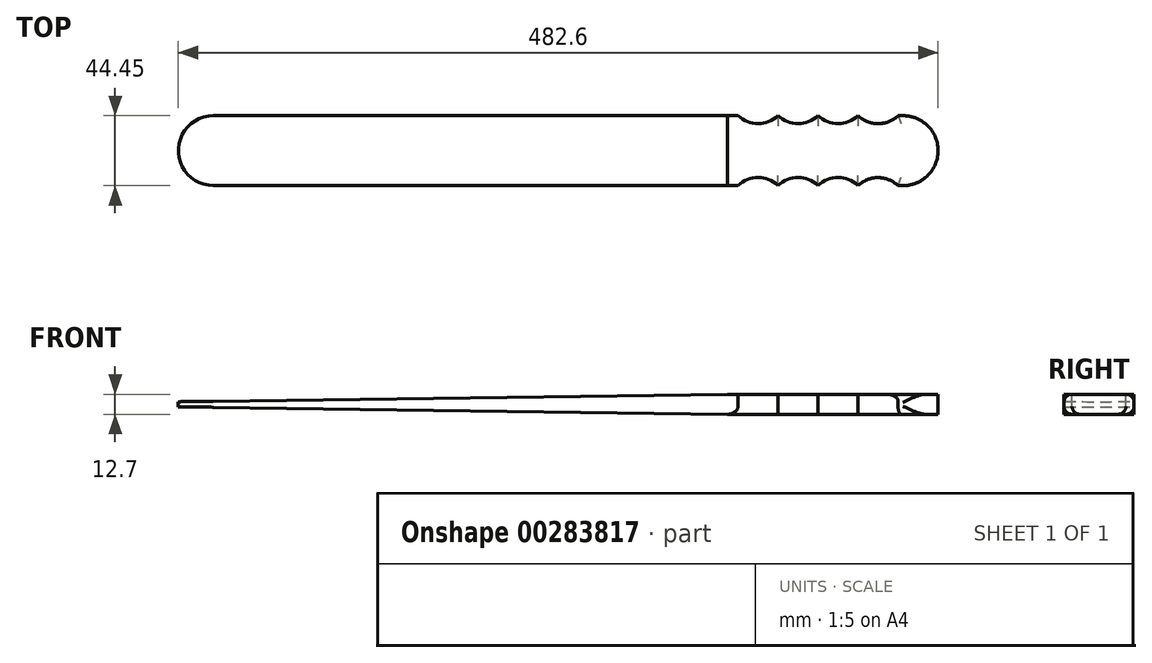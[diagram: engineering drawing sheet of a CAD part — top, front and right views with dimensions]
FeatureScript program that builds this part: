
annotation { "Feature Type Name" : "Feature", "Feature Type Description" : "" }
export const myFeature = defineFeature(function(context is Context, id is Id, definition is map)
    precondition{}
    {
        {
            var Q0;
            Q0=qCreatedBy(makeId("Front.planeOp"),FACE);
            var sketch = newSketch(context, id + "F0", { "sketchPlane" : qUnion([Q0])});
            skLineSegment(sketch, "E0", {"start": v(482.6, 6.35) * mm, "end": v(482.6, 0) * mm});
            skLineSegment(sketch, "E1.bottom", {"start": v(482.6, 6.35) * mm, "end": v(0, 6.35) * mm});
            skLineSegment(sketch, "E1.top", {"start": v(482.6, 0) * mm, "end": v(0, 0) * mm, "construction": true});
            skLineSegment(sketch, "E2", {"start": v(0, 6.35) * mm, "end": v(0, 0) * mm});
            skLineSegment(sketch, "E3.MirrorCS", {"start": v(482.6, -6.35) * mm, "end": v(482.6, 0) * mm});
            skLineSegment(sketch, "E4.MirrorCS", {"start": v(0, -6.35) * mm, "end": v(0, 0) * mm});
            skLineSegment(sketch, "E5.MirrorCS", {"start": v(482.6, -6.35) * mm, "end": v(0, -6.35) * mm});
            skSolve(sketch);
        }
        {
            var Q0;
            Q0 = qSketchRegion(id + "F0", true);
            extrude(context, id + "F1", {"entities" : qUnion([Q0]), "depth" : 44.45 * mm});
        }
        {
            var Q0;
            Q0=makeQuery(id+"F1.opExtrude","SWEPT_FACE",FACE,{"disambiguationData":[OSD([sQuery(id+"F0.wireOp",EDGE,"E1.bottom")])]});
            var sketch = newSketch(context, id + "F2", { "sketchPlane" : qUnion([Q0])});
            skLineSegment(sketch, "E6", {"start": v(355.6, 0) * mm, "end": v(355.6, -44.45) * mm, "construction": true});
            skArc(sketch, "E7", {"start": v(355.6, 0) * mm, "mid": v(368.3, -5.08) * mm, "end": v(381, 0) * mm});
            skLineSegment(sketch, "E8", {"start": v(355.6, -22.23) * mm, "end": v(482.6, -22.23) * mm, "construction": true});
            skArc(sketch, "E9.MirrorCS", {"start": v(355.6, -44.45) * mm, "mid": v(368.3, -39.37) * mm, "end": v(381, -44.45) * mm});
            skArc(sketch, "E10.1.0.0", {"start": v(381, 0) * mm, "mid": v(393.7, -5.08) * mm, "end": v(406.4, 0) * mm});
            skArc(sketch, "E10.1.0.1", {"start": v(381, -44.45) * mm, "mid": v(393.7, -39.37) * mm, "end": v(406.4, -44.45) * mm});
            skArc(sketch, "E10.2.0.0", {"start": v(406.4, 0) * mm, "mid": v(419.1, -5.08) * mm, "end": v(431.8, 0) * mm});
            skArc(sketch, "E10.2.0.1", {"start": v(406.4, -44.45) * mm, "mid": v(419.1, -39.37) * mm, "end": v(431.8, -44.45) * mm});
            skArc(sketch, "E10.3.0.0", {"start": v(431.8, 0) * mm, "mid": v(444.5, -5.08) * mm, "end": v(457.2, 0) * mm});
            skArc(sketch, "E10.3.0.1", {"start": v(431.8, -44.45) * mm, "mid": v(444.5, -39.37) * mm, "end": v(457.2, -44.45) * mm});
            skLineSegment(sketch, "E10.direction1", {"start": v(368.3, -57.79) * mm, "end": v(393.7, -57.79) * mm, "construction": true});
            skLineSegment(sketch, "E11", {"start": v(355.6, 0) * mm, "end": v(457.2, 0) * mm});
            skLineSegment(sketch, "E12.MirrorCS", {"start": v(355.6, -44.45) * mm, "end": v(457.2, -44.45) * mm});
            skSolve(sketch);
        }
        {
            var Q0;
            Q0 = qSketchRegion(id + "F2", true);
            extrude(context, id + "F3", {"entities" : qUnion([Q0]), "operationType" : NewBodyOperationType.REMOVE, "endBound" : BoundingType.THROUGH_ALL, "oppositeDirection" : true, "depth" : 25.4 * mm});
        }
        {
            var Q0;
            Q0=makeQuery(id+"F3.boolean.opBoolean","COPY",EDGE,{"derivedFrom":makeQuery(id+"F3.opExtrude","CAP_EDGE",EDGE,{"disambiguationData":[OSD([sQuery(id+"F2.wireOp",EDGE,"E9.MirrorCS")])],"isStart":true})});
            var Q1;
            Q1=makeQuery(id+"F3.boolean.opBoolean","COPY",EDGE,{"derivedFrom":makeQuery(id+"F3.opExtrude","CAP_EDGE",EDGE,{"disambiguationData":[OSD([sQuery(id+"F2.wireOp",EDGE,"E10.1.0.1")])],"isStart":true})});
            var Q2;
            Q2=makeQuery(id+"F3.boolean.opBoolean","COPY",EDGE,{"derivedFrom":makeQuery(id+"F3.opExtrude","CAP_EDGE",EDGE,{"disambiguationData":[OSD([sQuery(id+"F2.wireOp",EDGE,"E10.2.0.1")])],"isStart":true})});
            var Q3;
            Q3=makeQuery(id+"F3.boolean.opBoolean","COPY",EDGE,{"derivedFrom":makeQuery(id+"F3.opExtrude","CAP_EDGE",EDGE,{"disambiguationData":[OSD([sQuery(id+"F2.wireOp",EDGE,"E10.3.0.1")])],"isStart":true})});
            var Q4;
            Q4=makeQuery(id+"F3.boolean.opBoolean","COPY",EDGE,{"derivedFrom":makeQuery(id+"F3.opExtrude","CAP_EDGE",EDGE,{"disambiguationData":[OSD([sQuery(id+"F2.wireOp",EDGE,"E10.3.0.0")])],"isStart":true})});
            var Q5;
            Q5=makeQuery(id+"F3.boolean.opBoolean","COPY",EDGE,{"derivedFrom":makeQuery(id+"F3.opExtrude","CAP_EDGE",EDGE,{"disambiguationData":[OSD([sQuery(id+"F2.wireOp",EDGE,"E10.2.0.0")])],"isStart":true})});
            var Q6;
            Q6=makeQuery(id+"F3.boolean.opBoolean","COPY",EDGE,{"derivedFrom":makeQuery(id+"F3.opExtrude","CAP_EDGE",EDGE,{"disambiguationData":[OSD([sQuery(id+"F2.wireOp",EDGE,"E10.1.0.0")])],"isStart":true})});
            var Q7;
            Q7=makeQuery(id+"F3.boolean.opBoolean","COPY",EDGE,{"derivedFrom":makeQuery(id+"F3.opExtrude","CAP_EDGE",EDGE,{"disambiguationData":[OSD([sQuery(id+"F2.wireOp",EDGE,"E7")])],"isStart":true})});
            var Q8;
            Q8=makeQuery(id+"F3.boolean.opBoolean","INTERSECT",EDGE,{"derivedFrom":[makeQuery(id+"F1.opExtrude","SWEPT_FACE",FACE,{"disambiguationData":[OSD([sQuery(id+"F0.wireOp",EDGE,"E5.MirrorCS")])]}),makeQuery(id+"F3.opExtrude","SWEPT_FACE",FACE,{"disambiguationData":[OSD([sQuery(id+"F2.wireOp",EDGE,"E10.2.0.1")])]})]});
            var Q9;
            Q9=makeQuery(id+"F3.boolean.opBoolean","INTERSECT",EDGE,{"derivedFrom":[makeQuery(id+"F1.opExtrude","SWEPT_FACE",FACE,{"disambiguationData":[OSD([sQuery(id+"F0.wireOp",EDGE,"E5.MirrorCS")])]}),makeQuery(id+"F3.opExtrude","SWEPT_FACE",FACE,{"disambiguationData":[OSD([sQuery(id+"F2.wireOp",EDGE,"E10.1.0.1")])]})]});
            var Q10;
            Q10=makeQuery(id+"F3.boolean.opBoolean","INTERSECT",EDGE,{"derivedFrom":[makeQuery(id+"F1.opExtrude","SWEPT_FACE",FACE,{"disambiguationData":[OSD([sQuery(id+"F0.wireOp",EDGE,"E5.MirrorCS")])]}),makeQuery(id+"F3.opExtrude","SWEPT_FACE",FACE,{"disambiguationData":[OSD([sQuery(id+"F2.wireOp",EDGE,"E9.MirrorCS")])]})]});
            var Q11;
            Q11=makeQuery(id+"F3.boolean.opBoolean","INTERSECT",EDGE,{"derivedFrom":[makeQuery(id+"F1.opExtrude","SWEPT_FACE",FACE,{"disambiguationData":[OSD([sQuery(id+"F0.wireOp",EDGE,"E5.MirrorCS")])]}),makeQuery(id+"F3.opExtrude","SWEPT_FACE",FACE,{"disambiguationData":[OSD([sQuery(id+"F2.wireOp",EDGE,"E10.3.0.1")])]})]});
            var Q12;
            {var subQ0=sQuery(id+"F0.wireOp",EDGE,"E1.bottom");Q12=makeQuery(id+"F3.boolean.opBoolean","SPLIT",EDGE,{"disambiguationData":[TD([makeQuery(id+"F3.opExtrude","SWEPT_FACE",FACE,{"disambiguationData":[OSD([sQuery(id+"F2.wireOp",EDGE,"E10.3.0.1")])]})])],"derivedFrom":makeQuery(id+"F1.opExtrude","CAP_EDGE",EDGE,{"disambiguationData":[OSD([subQ0])],"isStart":false})});}
            var Q13;
            {var subQ0=sQuery(id+"F0.wireOp",EDGE,"E5.MirrorCS");Q13=makeQuery(id+"F3.boolean.opBoolean","SPLIT",EDGE,{"disambiguationData":[TD([makeQuery(id+"F3.opExtrude","SWEPT_FACE",FACE,{"disambiguationData":[OSD([sQuery(id+"F2.wireOp",EDGE,"E10.3.0.1")])]})])],"derivedFrom":makeQuery(id+"F1.opExtrude","CAP_EDGE",EDGE,{"disambiguationData":[OSD([subQ0])],"isStart":false})});}
            var Q14;
            {var subQ0=sQuery(id+"F0.wireOp",EDGE,"E1.bottom");Q14=makeQuery(id+"F3.boolean.opBoolean","SPLIT",EDGE,{"disambiguationData":[TD([makeQuery(id+"F3.opExtrude","SWEPT_FACE",FACE,{"disambiguationData":[OSD([sQuery(id+"F2.wireOp",EDGE,"E10.3.0.0")])]})])],"derivedFrom":makeQuery(id+"F1.opExtrude","CAP_EDGE",EDGE,{"disambiguationData":[OSD([subQ0])],"isStart":true})});}
            var Q15;
            {var subQ0=sQuery(id+"F0.wireOp",EDGE,"E5.MirrorCS");Q15=makeQuery(id+"F3.boolean.opBoolean","SPLIT",EDGE,{"disambiguationData":[TD([makeQuery(id+"F3.opExtrude","SWEPT_FACE",FACE,{"disambiguationData":[OSD([sQuery(id+"F2.wireOp",EDGE,"E10.3.0.0")])]})])],"derivedFrom":makeQuery(id+"F1.opExtrude","CAP_EDGE",EDGE,{"disambiguationData":[OSD([subQ0])],"isStart":true})});}
            var Q16;
            Q16=makeQuery(id+"F3.boolean.opBoolean","INTERSECT",EDGE,{"derivedFrom":[makeQuery(id+"F1.opExtrude","SWEPT_FACE",FACE,{"disambiguationData":[OSD([sQuery(id+"F0.wireOp",EDGE,"E5.MirrorCS")])]}),makeQuery(id+"F3.opExtrude","SWEPT_FACE",FACE,{"disambiguationData":[OSD([sQuery(id+"F2.wireOp",EDGE,"E10.3.0.0")])]})]});
            var Q17;
            Q17=makeQuery(id+"F3.boolean.opBoolean","INTERSECT",EDGE,{"derivedFrom":[makeQuery(id+"F1.opExtrude","SWEPT_FACE",FACE,{"disambiguationData":[OSD([sQuery(id+"F0.wireOp",EDGE,"E5.MirrorCS")])]}),makeQuery(id+"F3.opExtrude","SWEPT_FACE",FACE,{"disambiguationData":[OSD([sQuery(id+"F2.wireOp",EDGE,"E10.2.0.0")])]})]});
            var Q18;
            Q18=makeQuery(id+"F3.boolean.opBoolean","INTERSECT",EDGE,{"derivedFrom":[makeQuery(id+"F1.opExtrude","SWEPT_FACE",FACE,{"disambiguationData":[OSD([sQuery(id+"F0.wireOp",EDGE,"E5.MirrorCS")])]}),makeQuery(id+"F3.opExtrude","SWEPT_FACE",FACE,{"disambiguationData":[OSD([sQuery(id+"F2.wireOp",EDGE,"E10.1.0.0")])]})]});
            var Q19;
            Q19=makeQuery(id+"F3.boolean.opBoolean","INTERSECT",EDGE,{"derivedFrom":[makeQuery(id+"F1.opExtrude","SWEPT_FACE",FACE,{"disambiguationData":[OSD([sQuery(id+"F0.wireOp",EDGE,"E5.MirrorCS")])]}),makeQuery(id+"F3.opExtrude","SWEPT_FACE",FACE,{"disambiguationData":[OSD([sQuery(id+"F2.wireOp",EDGE,"E7")])]})]});
            fillet(context, id + "F4", {"entities" : qUnion([Q0, Q1, Q2, Q3, Q4, Q5, Q6, Q7, Q8, Q9, Q10, Q11, Q12, Q13, Q14, Q15, Q16, Q17, Q18, Q19]), "radius" : 5.08 * mm, "tangentPropagation" : true, "allowEdgeOverflow" : false});
        }
        {
            var Q0;
            {var subQ0=sQuery(id+"F0.wireOp",EDGE,"E1.bottom");var subQ1=sQuery(id+"F0.wireOp",EDGE,"E5.MirrorCS");var subQ2=sQuery(id+"F0.wireOp",EDGE,"E4.MirrorCS");var subQ3=sQuery(id+"F0.wireOp",EDGE,"E2");Q0=makeQuery(id+"F3.boolean.opBoolean","SPLIT",FACE,{"disambiguationData":[TD([makeQuery(id+"F3.opExtrude","SWEPT_FACE",FACE,{"disambiguationData":[OSD([sQuery(id+"F2.wireOp",EDGE,"E9.MirrorCS")])]})])],"derivedFrom":makeQuery(id+"F1.opExtrude","CAP_FACE",FACE,{"disambiguationData":[OSD([subQ0,sQuery(id+"F0.wireOp",EDGE,"E0"),subQ3,subQ2,sQuery(id+"F0.wireOp",EDGE,"E3.MirrorCS"),subQ1])],"isStart":false})});}
            var sketch = newSketch(context, id + "F5", { "sketchPlane" : qUnion([Q0])});
            skLineSegment(sketch, "E13", {"start": v(0, 0) * mm, "end": v(355.6, 0) * mm, "construction": true});
            skLineSegment(sketch, "E14", {"start": v(0, 0) * mm, "end": v(0, 1.59) * mm});
            skLineSegment(sketch, "E15", {"start": v(0, 1.59) * mm, "end": v(348.96, 6.35) * mm});
            skLineSegment(sketch, "E16.MirrorCS", {"start": v(0, 0) * mm, "end": v(0, -1.59) * mm});
            skLineSegment(sketch, "E17.MirrorCS", {"start": v(0, -1.59) * mm, "end": v(348.96, -6.35) * mm});
            skLineSegment(sketch, "E18.top", {"start": v(0, 6.35) * mm, "end": v(348.96, 6.35) * mm});
            skLineSegment(sketch, "E18.left", {"start": v(0, -6.35) * mm, "end": v(0, 6.35) * mm});
            skSolve(sketch);
        }
        {
            var Q0;
            {var subQ0=sQuery(id+"F5.wireOp",EDGE,"E15");Q0=makeQuery(id+"F5.imprint","IMPRINT",FACE,{"disambiguationData":[TD([[makeQuery(id+"F5.imprint","IMPRINT",EDGE,{"derivedFrom":subQ0}),1.0]])]});}
            var Q1;
            {var subQ0=sQuery(id+"F5.wireOp",EDGE,"E17.MirrorCS");Q1=makeQuery(id+"F5.imprint","IMPRINT",FACE,{"disambiguationData":[TD([[makeQuery(id+"F5.imprint","IMPRINT",EDGE,{"derivedFrom":subQ0}),-1.0]])]});}
            extrude(context, id + "F6", {"entities" : qUnion([Q0, Q1]), "operationType" : NewBodyOperationType.REMOVE, "endBound" : BoundingType.THROUGH_ALL, "oppositeDirection" : true, "depth" : 25.4 * mm});
        }
        {
            var Q0;
            Q0=qCreatedBy(makeId("Top.planeOp"),FACE);
            var sketch = newSketch(context, id + "F7", { "sketchPlane" : qUnion([Q0])});
            skArc(sketch, "E19", {"start": v(22.23, 0) * mm, "mid": v(0, -22.23) * mm, "end": v(22.23, -44.45) * mm});
            skLineSegment(sketch, "E20.bottom", {"start": v(0, 0) * mm, "end": v(22.23, 0) * mm});
            skLineSegment(sketch, "E20.top", {"start": v(0, -44.45) * mm, "end": v(22.23, -44.45) * mm});
            skLineSegment(sketch, "E20.left", {"start": v(0, 0) * mm, "end": v(0, -44.45) * mm});
            skArc(sketch, "E21", {"start": v(460.38, -44.45) * mm, "mid": v(482.6, -22.22) * mm, "end": v(460.38, 0) * mm});
            skLineSegment(sketch, "E22.bottom", {"start": v(482.6, 0) * mm, "end": v(460.38, 0) * mm});
            skLineSegment(sketch, "E22.top", {"start": v(482.6, -44.45) * mm, "end": v(460.38, -44.45) * mm});
            skLineSegment(sketch, "E22.left", {"start": v(482.6, 0) * mm, "end": v(482.6, -44.45) * mm});
            skPoint(sketch, "E23.orphan", {"position": v(244.17, -44.45) * mm});
            skSolve(sketch);
        }
        {
            var Q0;
            Q0 = qSketchRegion(id + "F7", true);
            extrude(context, id + "F8", {"entities" : qUnion([Q0]), "operationType" : NewBodyOperationType.REMOVE, "endBound" : BoundingType.SYMMETRIC, "oppositeDirection" : true, "depth" : 25.4 * mm});
        }
    });
